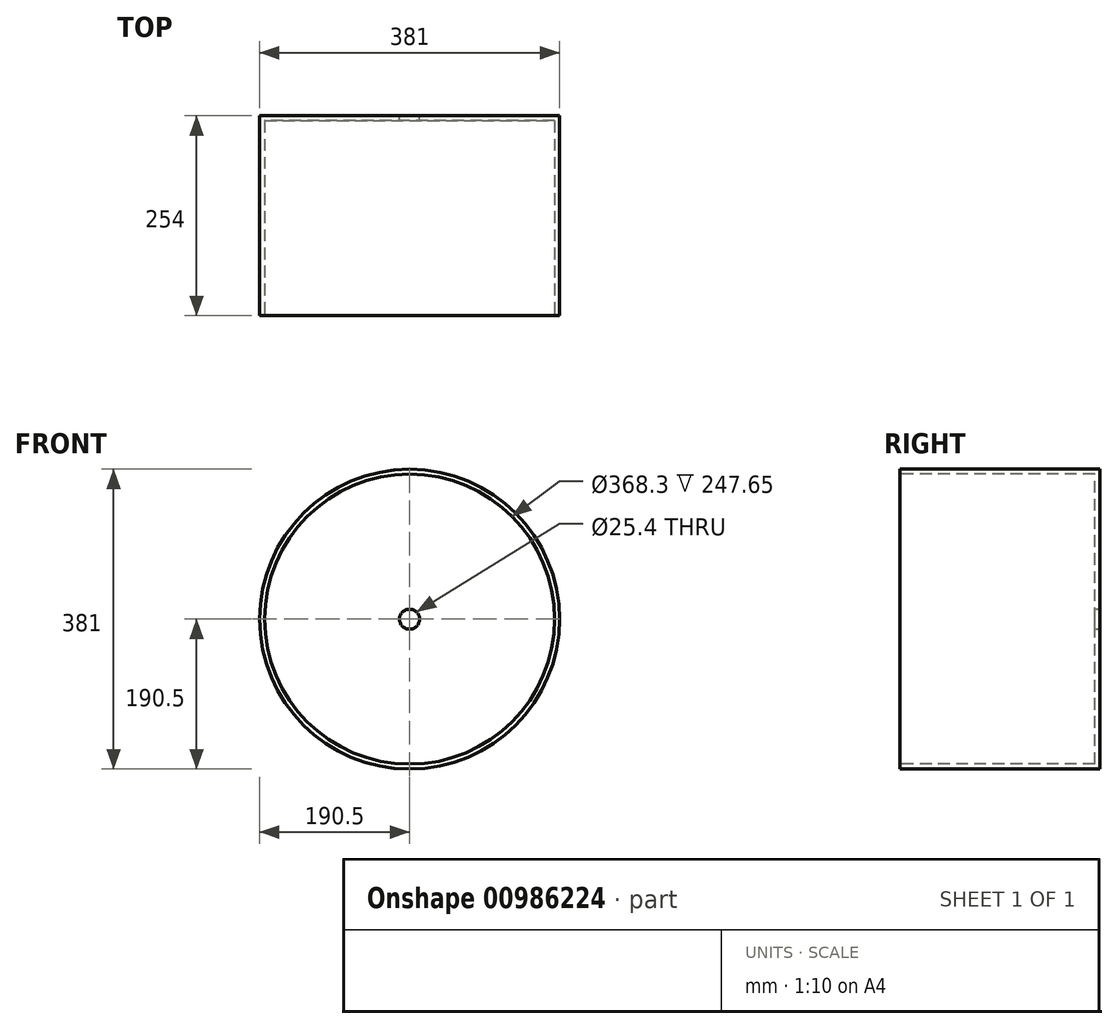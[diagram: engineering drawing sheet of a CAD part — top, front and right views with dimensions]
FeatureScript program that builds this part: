
annotation { "Feature Type Name" : "Feature", "Feature Type Description" : "" }
export const myFeature = defineFeature(function(context is Context, id is Id, definition is map)
    precondition{}
    {
        {
            var Q0;
            Q0=qCreatedBy(makeId("Front.planeOp"),FACE);
            var sketch = newSketch(context, id + "F0", { "sketchPlane" : qUnion([Q0])});
            skCircle(sketch, "E0", {"center": v(0, 0) * mm, "radius": 190.5 * mm});
            skSolve(sketch);
        }
        {
            var Q0;
            Q0=makeQuery(id+"F0.imprint","IMPRINT",FACE,{"disambiguationData":[TD([[makeQuery(id+"F0.imprint","IMPRINT",EDGE,{"derivedFrom":sQuery(id+"F0.wireOp",EDGE,"E0")}),1.0]])]});
            extrude(context, id + "F1", {"entities" : qUnion([Q0]), "depth" : 254 * mm, "offsetDistance" : 25.4 * mm});
        }
        {
            var Q0;
            Q0=makeQuery(id+"F1.opExtrude","CAP_FACE",FACE,{"disambiguationData":[OSD([sQuery(id+"F0.wireOp",EDGE,"E0")])],"isStart":false});
            var sketch = newSketch(context, id + "F2", { "sketchPlane" : qUnion([Q0])});
            skCircle(sketch, "E1.0", {"center": v(0, 0) * mm, "radius": 184.15 * mm});
            skSolve(sketch);
        }
        {
            var Q0;
            Q0=makeQuery(id+"F2.imprint","IMPRINT",FACE,{"disambiguationData":[TD([[makeQuery(id+"F2.imprint","IMPRINT",EDGE,{"derivedFrom":sQuery(id+"F2.wireOp",EDGE,"E1.0")}),1.0]])]});
            extrude(context, id + "F3", {"entities" : qUnion([Q0]), "operationType" : NewBodyOperationType.REMOVE, "oppositeDirection" : true, "depth" : 247.65 * mm, "offsetDistance" : 25.4 * mm});
        }
        {
            var Q0;
            Q0=makeQuery(id+"F1.opExtrude","CAP_FACE",FACE,{"disambiguationData":[OSD([sQuery(id+"F0.wireOp",EDGE,"E0")])],"isStart":true});
            var sketch = newSketch(context, id + "F4", { "sketchPlane" : qUnion([Q0])});
            skCircle(sketch, "E2", {"center": v(0, 0) * mm, "radius": 12.7 * mm});
            skSolve(sketch);
        }
        {
            var Q0;
            Q0=makeQuery(id+"F4.imprint","IMPRINT",FACE,{"disambiguationData":[TD([[makeQuery(id+"F4.imprint","IMPRINT",EDGE,{"derivedFrom":sQuery(id+"F4.wireOp",EDGE,"E2")}),1.0]])]});
            extrude(context, id + "F5", {"entities" : qUnion([Q0]), "operationType" : NewBodyOperationType.REMOVE, "endBound" : BoundingType.THROUGH_ALL, "oppositeDirection" : true, "depth" : 25.4 * mm, "offsetDistance" : 25.4 * mm});
        }
    });
